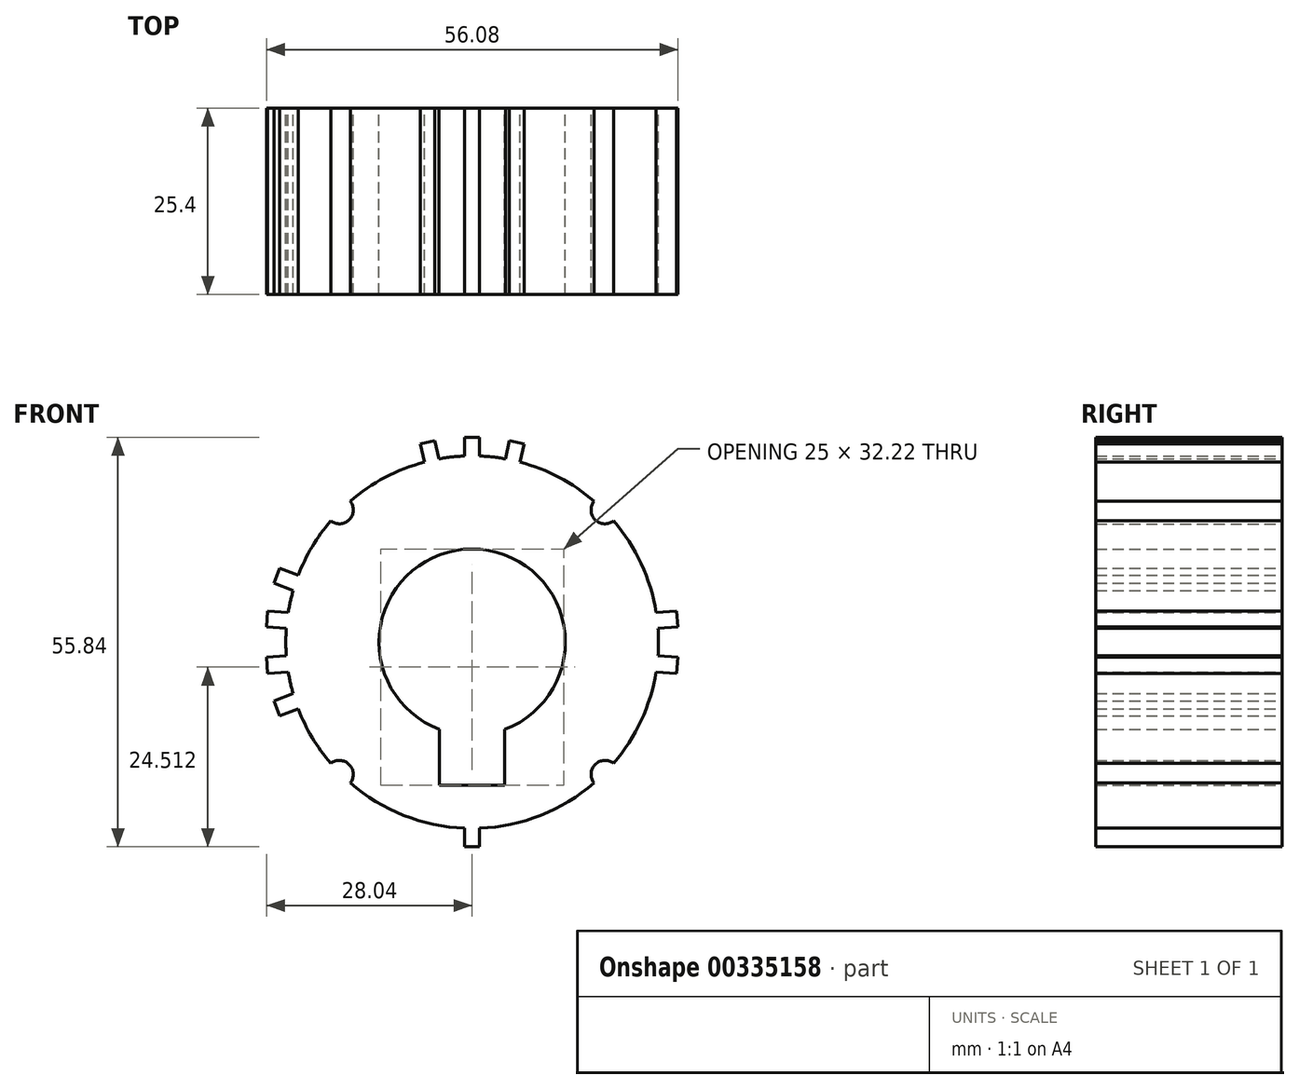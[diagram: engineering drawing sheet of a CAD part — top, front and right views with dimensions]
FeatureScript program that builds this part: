
annotation { "Feature Type Name" : "Feature", "Feature Type Description" : "" }
export const myFeature = defineFeature(function(context is Context, id is Id, definition is map)
    precondition{}
    {
        {
            var Q0;
            Q0=qCreatedBy(makeId("Front.planeOp"),FACE);
            var sketch = newSketch(context, id + "F0", { "sketchPlane" : qUnion([Q0])});
            skArc(sketch, "E0", {"start": v(16.62, 19.21) * mm, "mid": v(11.87, 22.46) * mm, "end": v(6.52, 24.55) * mm});
            skArc(sketch, "E1", {"start": v(-4.44, 11.9) * mm, "mid": v(-12.7, 0) * mm, "end": v(-4.44, -11.9) * mm});
            skArc(sketch, "E2", {"start": v(16.62, 19.21) * mm, "mid": v(16.76, 16.69) * mm, "end": v(19.28, 16.53) * mm});
            skPoint(sketch, "E3.end.orphan", {"position": v(0, 38.1) * mm});
            skPoint(sketch, "E4.end.orphan", {"position": v(38.1, 0) * mm});
            skArc(sketch, "E5.MirrorCS", {"start": v(-16.62, 19.21) * mm, "mid": v(-16.76, 16.69) * mm, "end": v(-19.28, 16.53) * mm});
            skArc(sketch, "E6.MirrorCS", {"start": v(16.62, -19.21) * mm, "mid": v(16.76, -16.69) * mm, "end": v(19.28, -16.53) * mm});
            skArc(sketch, "E7.MirrorCS", {"start": v(-16.62, -19.21) * mm, "mid": v(-16.76, -16.69) * mm, "end": v(-19.28, -16.53) * mm});
            skArc(sketch, "E8.trimOffspring", {"start": v(19.28, -16.53) * mm, "mid": v(23.04, -10.7) * mm, "end": v(25.07, -4.06) * mm});
            skArc(sketch, "E9.trimOffspring", {"start": v(-19.28, 16.53) * mm, "mid": v(-21.82, 13) * mm, "end": v(-23.71, 9.1) * mm});
            skArc(sketch, "E10.trimOffspring", {"start": v(-16.62, -19.21) * mm, "mid": v(-9.34, -23.62) * mm, "end": v(-1.02, -25.38) * mm});
            skLineSegment(sketch, "E11", {"start": v(1.02, 25.38) * mm, "end": v(1.02, 27.92) * mm});
            skLineSegment(sketch, "E12.MirrorCS", {"start": v(-1.02, 25.38) * mm, "end": v(-1.02, 27.92) * mm});
            skLineSegment(sketch, "E13", {"start": v(1.02, 27.92) * mm, "end": v(-1.02, 27.92) * mm});
            skArc(sketch, "E14.trimOffspring", {"start": v(-1.02, 25.38) * mm, "mid": v(-2.78, 25.25) * mm, "end": v(-4.53, 25) * mm});
            skLineSegment(sketch, "E15.MirrorCS", {"start": v(4.53, 25) * mm, "end": v(5.09, 27.47) * mm});
            skLineSegment(sketch, "E16.MirrorCS", {"start": v(5.09, 27.47) * mm, "end": v(7.07, 27.03) * mm});
            skLineSegment(sketch, "E17.MirrorCS", {"start": v(6.52, 24.55) * mm, "end": v(7.07, 27.03) * mm});
            skLineSegment(sketch, "E18.MirrorCS", {"start": v(-4.53, 25) * mm, "end": v(-5.09, 27.47) * mm});
            skLineSegment(sketch, "E19.MirrorCS", {"start": v(-6.52, 24.55) * mm, "end": v(-7.07, 27.03) * mm});
            skLineSegment(sketch, "E20.MirrorCS", {"start": v(-5.09, 27.47) * mm, "end": v(-7.07, 27.03) * mm});
            skArc(sketch, "E21.trimOffspring", {"start": v(4.53, 25) * mm, "mid": v(2.78, 25.25) * mm, "end": v(1.02, 25.38) * mm});
            skArc(sketch, "E22.trimOffspring", {"start": v(-6.52, 24.55) * mm, "mid": v(-11.87, 22.46) * mm, "end": v(-16.62, 19.21) * mm});
            skLineSegment(sketch, "E23.MirrorCS", {"start": v(1.02, -25.38) * mm, "end": v(1.02, -27.92) * mm});
            skLineSegment(sketch, "E24.MirrorCS", {"start": v(1.02, -27.92) * mm, "end": v(-1.02, -27.92) * mm});
            skLineSegment(sketch, "E25.MirrorCS", {"start": v(-1.02, -25.38) * mm, "end": v(-1.02, -27.92) * mm});
            skArc(sketch, "E26.trimOffspring", {"start": v(1.02, -25.38) * mm, "mid": v(9.34, -23.62) * mm, "end": v(16.62, -19.21) * mm});
            skLineSegment(sketch, "E27", {"start": v(28.04, -2.06) * mm, "end": v(27.88, -4.26) * mm});
            skLineSegment(sketch, "E28", {"start": v(27.88, -4.26) * mm, "end": v(25.07, -4.06) * mm});
            skLineSegment(sketch, "E29.trimOffspring", {"start": v(25.33, -1.86) * mm, "end": v(28.04, -2.06) * mm});
            skArc(sketch, "E30.trimOffspring", {"start": v(25.33, -1.86) * mm, "mid": v(25.4, 0) * mm, "end": v(25.33, 1.86) * mm});
            skLineSegment(sketch, "E31.MirrorCS", {"start": v(25.33, 1.86) * mm, "end": v(28.04, 2.06) * mm});
            skLineSegment(sketch, "E32.MirrorCS", {"start": v(28.04, 2.06) * mm, "end": v(27.88, 4.26) * mm});
            skLineSegment(sketch, "E33.MirrorCS", {"start": v(27.88, 4.26) * mm, "end": v(25.07, 4.06) * mm});
            skArc(sketch, "E34.trimOffspring", {"start": v(25.07, 4.06) * mm, "mid": v(23.04, 10.7) * mm, "end": v(19.28, 16.53) * mm});
            skLineSegment(sketch, "E35.MirrorCS", {"start": v(-27.88, -4.26) * mm, "end": v(-25.07, -4.06) * mm});
            skLineSegment(sketch, "E36.MirrorCS", {"start": v(-28.04, -2.06) * mm, "end": v(-27.88, -4.26) * mm});
            skLineSegment(sketch, "E37.MirrorCS", {"start": v(-25.33, -1.86) * mm, "end": v(-28.04, -2.06) * mm});
            skLineSegment(sketch, "E38.MirrorCS", {"start": v(-25.33, 1.86) * mm, "end": v(-28.04, 2.06) * mm});
            skLineSegment(sketch, "E39.MirrorCS", {"start": v(-28.04, 2.06) * mm, "end": v(-27.88, 4.26) * mm});
            skLineSegment(sketch, "E40.MirrorCS", {"start": v(-27.88, 4.26) * mm, "end": v(-25.07, 4.06) * mm});
            skLineSegment(sketch, "E41.MirrorCS", {"start": v(-27.04, -8.02) * mm, "end": v(-24.41, -7.01) * mm});
            skLineSegment(sketch, "E42.MirrorCS", {"start": v(-26.25, -10.08) * mm, "end": v(-27.04, -8.02) * mm});
            skLineSegment(sketch, "E43.MirrorCS", {"start": v(-23.71, -9.1) * mm, "end": v(-26.25, -10.08) * mm});
            skArc(sketch, "E44.trimOffspring", {"start": v(-23.71, -9.1) * mm, "mid": v(-21.82, -13) * mm, "end": v(-19.28, -16.53) * mm});
            skArc(sketch, "E45.trimOffspring", {"start": v(-25.07, -4.06) * mm, "mid": v(-24.79, -5.54) * mm, "end": v(-24.41, -7.01) * mm});
            skArc(sketch, "E46.trimOffspring", {"start": v(-25.33, 1.86) * mm, "mid": v(-25.4, 0) * mm, "end": v(-25.33, -1.86) * mm});
            skLineSegment(sketch, "E47.MirrorCS", {"start": v(-27.04, 8.02) * mm, "end": v(-24.41, 7.01) * mm});
            skLineSegment(sketch, "E48.MirrorCS", {"start": v(-26.25, 10.08) * mm, "end": v(-27.04, 8.02) * mm});
            skLineSegment(sketch, "E49.MirrorCS", {"start": v(-23.71, 9.1) * mm, "end": v(-26.25, 10.08) * mm});
            skArc(sketch, "E50.trimOffspring", {"start": v(-24.41, 7.01) * mm, "mid": v(-24.79, 5.54) * mm, "end": v(-25.07, 4.06) * mm});
            skArc(sketch, "E51", {"start": v(4.44, -11.9) * mm, "mid": v(0, 12.7) * mm, "end": v(-4.45, -11.9) * mm});
            skLineSegment(sketch, "E52.MirrorCS", {"start": v(4.45, -11.9) * mm, "end": v(4.45, -19.52) * mm});
            skLineSegment(sketch, "E53.MirrorCS", {"start": v(-4.44, -19.52) * mm, "end": v(4.44, -19.52) * mm});
            skLineSegment(sketch, "E54.MirrorCS", {"start": v(-4.44, -11.9) * mm, "end": v(-4.44, -19.52) * mm});
            skPoint(sketch, "E55.start.orphan", {"position": v(-4.44, 19.52) * mm});
            skPoint(sketch, "E56.MirrorCS.end.orphan", {"position": v(4.45, 19.52) * mm});
            skArc(sketch, "E57.trimOffspring", {"start": v(4.44, -11.9) * mm, "mid": v(12.7, 0) * mm, "end": v(4.44, 11.9) * mm});
            skSolve(sketch);
        }
        {
            var Q0;
            Q0=qSketchRegion(id+"F0",true);
            extrude(context, id + "F1", {"entities" : qUnion([Q0]), "depth" : 25.4 * mm, "offsetDistance" : 25.4 * mm});
        }
    });
